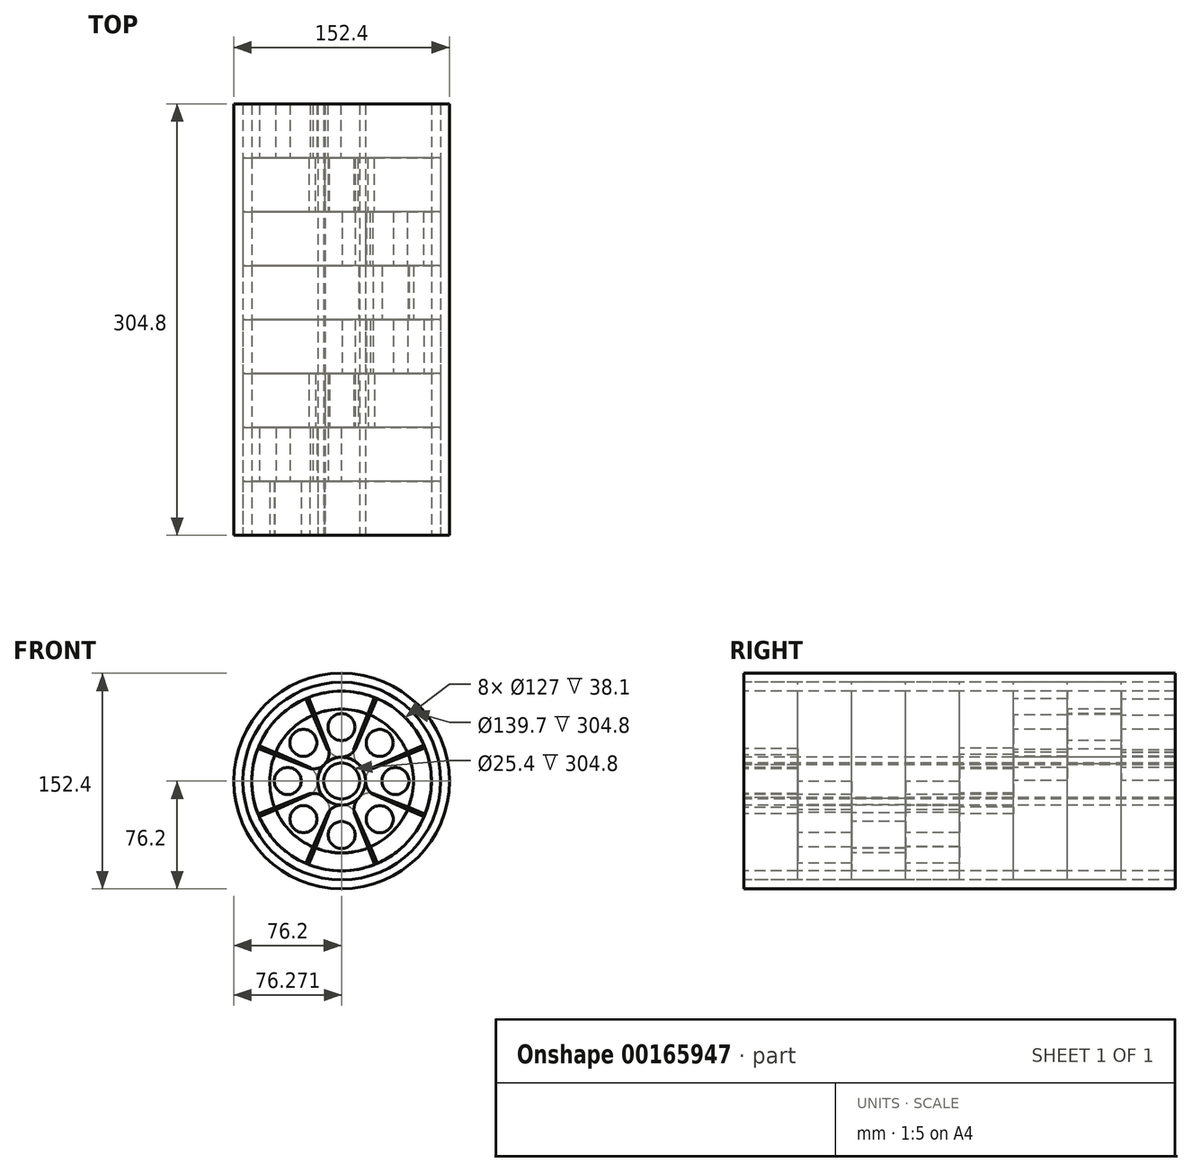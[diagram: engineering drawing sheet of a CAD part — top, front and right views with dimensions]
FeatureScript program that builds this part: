
annotation { "Feature Type Name" : "Feature", "Feature Type Description" : "" }
export const myFeature = defineFeature(function(context is Context, id is Id, definition is map)
    precondition{}
    {
        {
            var Q0;
            Q0=qCreatedBy(makeId("Front.planeOp"),FACE);
            var sketch = newSketch(context, id + "F0", { "sketchPlane" : qUnion([Q0])});
            skCircle(sketch, "E0", {"center": v(0, 0) * mm, "radius": 76.2 * mm});
            skCircle(sketch, "E1", {"center": v(0, 0) * mm, "radius": 63.5 * mm});
            skLineSegment(sketch, "E2", {"start": v(-47.23, -18.71) * mm, "end": v(-59.03, -23.4) * mm});
            skLineSegment(sketch, "E3", {"start": v(-47.15, 18.5) * mm, "end": v(-59.03, 23.21) * mm});
            skArc(sketch, "E4", {"start": v(-59.03, 23.21) * mm, "mid": v(-63.46, -0.1) * mm, "end": v(-59.03, -23.4) * mm});
            skArc(sketch, "E5", {"start": v(-47.15, 18.5) * mm, "mid": v(-50.76, -0.1) * mm, "end": v(-47.23, -18.71) * mm});
            skCircle(sketch, "E6", {"center": v(0.04, -0.1) * mm, "radius": 16.9 * mm});
            skLineSegment(sketch, "E7", {"start": v(-47.23, -18.71) * mm, "end": v(-15.66, -6.32) * mm});
            skLineSegment(sketch, "E8", {"start": v(-47.15, 18.5) * mm, "end": v(-15.65, 6.16) * mm});
            skCircle(sketch, "E9", {"center": v(0, 0) * mm, "radius": 12.7 * mm});
            skPoint(sketch, "E10.middle", {"position": v(-34.7, 0) * mm});
            skArc(sketch, "E11", {"start": v(-22.37, 8.8) * mm, "mid": v(-16.55, 9.06) * mm, "end": v(-11.6, 12.14) * mm});
            skArc(sketch, "E12", {"start": v(-11.6, -12.34) * mm, "mid": v(-16.54, -9.23) * mm, "end": v(-22.37, -8.95) * mm});
            skArc(sketch, "E13", {"start": v(-58.86, 23.14) * mm, "mid": v(-63.24, -0.1) * mm, "end": v(-58.8, -23.31) * mm});
            skCircle(sketch, "E14", {"center": v(-38.06, 0) * mm, "radius": 9.53 * mm});
            skCircle(sketch, "E15", {"center": v(0.07, 0) * mm, "radius": 69.85 * mm});
            skSolve(sketch);
        }
        {
            var Q0;
            Q0=makeQuery(id+"F0.imprint","IMPRINT",FACE,{"disambiguationData":[TD([[makeQuery(id+"F0.imprint","IMPRINT",EDGE,{"derivedFrom":sQuery(id+"F0.wireOp",EDGE,"dWqBjylU-pobx-G8Ro-5PX9-iFVg2W9Lq8eQ")}),1.0]])]});
            var Q1;
            Q1=makeQuery(id+"F0.imprint","IMPRINT",FACE,{"disambiguationData":[TD([[makeQuery(id+"F0.imprint","IMPRINT",EDGE,{"derivedFrom":sQuery(id+"F0.wireOp",EDGE,"E0")}),1.0]])]});
            extrude(context, id + "F1", {"entities" : qUnion([Q0, Q1]), "oppositeDirection" : true, "depth" : 304.8 * mm});
        }
        {
            var Q0;
            Q0=makeQuery(id+"F0.imprint","IMPRINT",FACE,{"disambiguationData":[TD([[makeQuery(id+"F0.imprint","IMPRINT",EDGE,{"derivedFrom":sQuery(id+"F0.wireOp",EDGE,"E2")}),-1.0]])]});
            extrude(context, id + "F2", {"entities" : qUnion([Q0]), "oppositeDirection" : true, "depth" : 38.1 * mm});
        }
        {
            var Q0;
            Q0=makeQuery(id+"F2.opExtrude","SWEPT_BODY",BODY,{"disambiguationData":[OSD([sQuery(id+"F0.wireOp",EDGE,"E2"),sQuery(id+"F0.wireOp",EDGE,"E3"),sQuery(id+"F0.wireOp",EDGE,"E4"),sQuery(id+"F0.wireOp",EDGE,"E5")])]});
            var Q1;
            Q1=makeQuery(id+"F1.opExtrude","CAP_EDGE",EDGE,{"disambiguationData":[OSD([sQuery(id+"F0.wireOp",EDGE,"E1")])],"isStart":true});
            transform(context, id + "F3", {"entities" : qUnion([Q0]), "transformType" : TransformType.TRANSLATION_3D, "dx" : 0 * mm, "dy" : 38.1 * mm, "dz" : 0 * mm, "makeCopy" : true});
        }
        {
            var Q0;
            Q0=makeQuery(id+"F3.opPattern","COPY",BODY,{"derivedFrom":makeQuery(id+"F2.opExtrude","SWEPT_BODY",BODY,{"disambiguationData":[OSD([sQuery(id+"F0.wireOp",EDGE,"E2"),sQuery(id+"F0.wireOp",EDGE,"E3"),sQuery(id+"F0.wireOp",EDGE,"E4"),sQuery(id+"F0.wireOp",EDGE,"E5")])]}),"instanceName":"1"});
            var Q1;
            Q1=makeQuery(id+"F1.opExtrude","CAP_EDGE",EDGE,{"disambiguationData":[OSD([sQuery(id+"F0.wireOp",EDGE,"E15")])],"isStart":true});
            transform(context, id + "F4", {"entities" : qUnion([Q0]), "transformType" : TransformType.ROTATION, "transformAxis" : qUnion([Q1]), "angle" : 45 * degree, "makeCopy" : false});
        }
        {
            var Q0;
            Q0=makeQuery(id+"F2.opExtrude","SWEPT_BODY",BODY,{"disambiguationData":[OSD([sQuery(id+"F0.wireOp",EDGE,"E2"),sQuery(id+"F0.wireOp",EDGE,"E3"),sQuery(id+"F0.wireOp",EDGE,"E4"),sQuery(id+"F0.wireOp",EDGE,"E5")])]});
            var Q1;
            Q1=makeQuery(id+"F3.opPattern","COPY",BODY,{"derivedFrom":makeQuery(id+"F2.opExtrude","SWEPT_BODY",BODY,{"disambiguationData":[OSD([sQuery(id+"F0.wireOp",EDGE,"E2"),sQuery(id+"F0.wireOp",EDGE,"E3"),sQuery(id+"F0.wireOp",EDGE,"E4"),sQuery(id+"F0.wireOp",EDGE,"E5")])]}),"instanceName":"1"});
            transform(context, id + "F5", {"entities" : qUnion([Q0, Q1]), "transformType" : TransformType.TRANSLATION_3D, "dx" : 0 * mm, "dy" : 76.2 * mm, "dz" : 0 * mm, "makeCopy" : true});
        }
        {
            var Q0;
            Q0=makeQuery(id+"F5.opPattern","COPY",BODY,{"derivedFrom":makeQuery(id+"F2.opExtrude","SWEPT_BODY",BODY,{"disambiguationData":[OSD([sQuery(id+"F0.wireOp",EDGE,"E2"),sQuery(id+"F0.wireOp",EDGE,"E3"),sQuery(id+"F0.wireOp",EDGE,"E4"),sQuery(id+"F0.wireOp",EDGE,"E5")])]}),"instanceName":"1"});
            var Q1;
            Q1=makeQuery(id+"F5.opPattern","COPY",BODY,{"derivedFrom":makeQuery(id+"F3.opPattern","COPY",BODY,{"derivedFrom":makeQuery(id+"F2.opExtrude","SWEPT_BODY",BODY,{"disambiguationData":[OSD([sQuery(id+"F0.wireOp",EDGE,"E2"),sQuery(id+"F0.wireOp",EDGE,"E3"),sQuery(id+"F0.wireOp",EDGE,"E4"),sQuery(id+"F0.wireOp",EDGE,"E5")])]}),"instanceName":"1"}),"instanceName":"1"});
            var Q2;
            Q2=makeQuery(id+"F1.opExtrude","CAP_EDGE",EDGE,{"disambiguationData":[OSD([sQuery(id+"F0.wireOp",EDGE,"E0")])],"isStart":true});
            transform(context, id + "F6", {"entities" : qUnion([Q0, Q1]), "transformType" : TransformType.ROTATION, "transformAxis" : qUnion([Q2]), "angle" : 90 * degree, "makeCopy" : false});
        }
        {
            var Q0;
            Q0=makeQuery(id+"F2.opExtrude","SWEPT_BODY",BODY,{"disambiguationData":[OSD([sQuery(id+"F0.wireOp",EDGE,"E2"),sQuery(id+"F0.wireOp",EDGE,"E3"),sQuery(id+"F0.wireOp",EDGE,"E4"),sQuery(id+"F0.wireOp",EDGE,"E5")])]});
            var Q1;
            Q1=makeQuery(id+"F3.opPattern","COPY",BODY,{"derivedFrom":makeQuery(id+"F2.opExtrude","SWEPT_BODY",BODY,{"disambiguationData":[OSD([sQuery(id+"F0.wireOp",EDGE,"E2"),sQuery(id+"F0.wireOp",EDGE,"E3"),sQuery(id+"F0.wireOp",EDGE,"E4"),sQuery(id+"F0.wireOp",EDGE,"E5")])]}),"instanceName":"1"});
            var Q2;
            Q2=makeQuery(id+"F5.opPattern","COPY",BODY,{"derivedFrom":makeQuery(id+"F2.opExtrude","SWEPT_BODY",BODY,{"disambiguationData":[OSD([sQuery(id+"F0.wireOp",EDGE,"E2"),sQuery(id+"F0.wireOp",EDGE,"E3"),sQuery(id+"F0.wireOp",EDGE,"E4"),sQuery(id+"F0.wireOp",EDGE,"E5")])]}),"instanceName":"1"});
            var Q3;
            Q3=makeQuery(id+"F5.opPattern","COPY",BODY,{"derivedFrom":makeQuery(id+"F3.opPattern","COPY",BODY,{"derivedFrom":makeQuery(id+"F2.opExtrude","SWEPT_BODY",BODY,{"disambiguationData":[OSD([sQuery(id+"F0.wireOp",EDGE,"E2"),sQuery(id+"F0.wireOp",EDGE,"E3"),sQuery(id+"F0.wireOp",EDGE,"E4"),sQuery(id+"F0.wireOp",EDGE,"E5")])]}),"instanceName":"1"}),"instanceName":"1"});
            transform(context, id + "F7", {"entities" : qUnion([Q0, Q1, Q2, Q3]), "transformType" : TransformType.TRANSLATION_3D, "dx" : 0 * mm, "dy" : 152.4 * mm, "dz" : 0 * mm, "makeCopy" : true});
        }
        {
            var Q0;
            Q0=makeQuery(id+"F7.opPattern","COPY",BODY,{"derivedFrom":makeQuery(id+"F2.opExtrude","SWEPT_BODY",BODY,{"disambiguationData":[OSD([sQuery(id+"F0.wireOp",EDGE,"E2"),sQuery(id+"F0.wireOp",EDGE,"E3"),sQuery(id+"F0.wireOp",EDGE,"E4"),sQuery(id+"F0.wireOp",EDGE,"E5")])]}),"instanceName":"1"});
            var Q1;
            Q1=makeQuery(id+"F7.opPattern","COPY",BODY,{"derivedFrom":makeQuery(id+"F3.opPattern","COPY",BODY,{"derivedFrom":makeQuery(id+"F2.opExtrude","SWEPT_BODY",BODY,{"disambiguationData":[OSD([sQuery(id+"F0.wireOp",EDGE,"E2"),sQuery(id+"F0.wireOp",EDGE,"E3"),sQuery(id+"F0.wireOp",EDGE,"E4"),sQuery(id+"F0.wireOp",EDGE,"E5")])]}),"instanceName":"1"}),"instanceName":"1"});
            var Q2;
            Q2=makeQuery(id+"F7.opPattern","COPY",BODY,{"derivedFrom":makeQuery(id+"F5.opPattern","COPY",BODY,{"derivedFrom":makeQuery(id+"F2.opExtrude","SWEPT_BODY",BODY,{"disambiguationData":[OSD([sQuery(id+"F0.wireOp",EDGE,"E2"),sQuery(id+"F0.wireOp",EDGE,"E3"),sQuery(id+"F0.wireOp",EDGE,"E4"),sQuery(id+"F0.wireOp",EDGE,"E5")])]}),"instanceName":"1"}),"instanceName":"1"});
            var Q3;
            Q3=makeQuery(id+"F7.opPattern","COPY",BODY,{"derivedFrom":makeQuery(id+"F5.opPattern","COPY",BODY,{"derivedFrom":makeQuery(id+"F3.opPattern","COPY",BODY,{"derivedFrom":makeQuery(id+"F2.opExtrude","SWEPT_BODY",BODY,{"disambiguationData":[OSD([sQuery(id+"F0.wireOp",EDGE,"E2"),sQuery(id+"F0.wireOp",EDGE,"E3"),sQuery(id+"F0.wireOp",EDGE,"E4"),sQuery(id+"F0.wireOp",EDGE,"E5")])]}),"instanceName":"1"}),"instanceName":"1"}),"instanceName":"1"});
            var Q4;
            Q4=makeQuery(id+"F1.opExtrude","CAP_EDGE",EDGE,{"disambiguationData":[OSD([sQuery(id+"F0.wireOp",EDGE,"E0")])],"isStart":true});
            transform(context, id + "F8", {"entities" : qUnion([Q0, Q1, Q2, Q3]), "transformType" : TransformType.ROTATION, "transformAxis" : qUnion([Q4]), "angle" : 180 * degree, "makeCopy" : false});
        }
        {
            var Q0;
            Q0=makeQuery(id+"F0.imprint","IMPRINT",FACE,{"disambiguationData":[TD([[makeQuery(id+"F0.imprint","IMPRINT",EDGE,{"derivedFrom":sQuery(id+"F0.wireOp",EDGE,"E5")}),1.0]])]});
            var Q1;
            {var subQ0=sQuery(id+"F0.wireOp",EDGE,"E8");var subQ1=sQuery(id+"F0.wireOp",EDGE,"E6");var subQ2=makeQuery(id+"F0.imprint","INTERSECT",VERTEX,{"derivedFrom":[subQ1,subQ0]});Q1=makeQuery(id+"F0.imprint","IMPRINT",FACE,{"disambiguationData":[TD([[makeQuery(id+"F0.imprint","IMPRINT",EDGE,{"disambiguationData":[TD([[subQ2,1.0]])],"derivedFrom":subQ1}),-1.0]])]});}
            var Q2;
            {var subQ0=sQuery(id+"F0.wireOp",EDGE,"E7");var subQ1=sQuery(id+"F0.wireOp",EDGE,"E6");var subQ2=makeQuery(id+"F0.imprint","INTERSECT",VERTEX,{"derivedFrom":[subQ1,subQ0]});Q2=makeQuery(id+"F0.imprint","IMPRINT",FACE,{"disambiguationData":[TD([[makeQuery(id+"F0.imprint","IMPRINT",EDGE,{"disambiguationData":[TD([[subQ2,-1.0]])],"derivedFrom":subQ1}),-1.0]])]});}
            extrude(context, id + "F9", {"entities" : qUnion([Q0, Q1, Q2]), "oppositeDirection" : true, "depth" : 38.1 * mm});
        }
        {
            var Q0;
            Q0=makeQuery(id+"F9.opExtrude","SWEPT_BODY",BODY,{"disambiguationData":[OSD([sQuery(id+"F0.wireOp",EDGE,"E5"),sQuery(id+"F0.wireOp",EDGE,"E6"),sQuery(id+"F0.wireOp",EDGE,"E7"),sQuery(id+"F0.wireOp",EDGE,"E8"),sQuery(id+"F0.wireOp",EDGE,"4N7eOMkn-36Zl-0K50-I79r-F5F3qFzNZoCP"),sQuery(id+"F0.wireOp",EDGE,"E11"),sQuery(id+"F0.wireOp",EDGE,"E12")])]});
            transform(context, id + "F10", {"entities" : qUnion([Q0]), "transformType" : TransformType.TRANSLATION_3D, "dx" : 0 * mm, "dy" : 38.1 * mm, "dz" : 0 * mm, "makeCopy" : true});
        }
        {
            var Q0;
            Q0=makeQuery(id+"F10.opPattern","COPY",BODY,{"derivedFrom":makeQuery(id+"F9.opExtrude","SWEPT_BODY",BODY,{"disambiguationData":[OSD([sQuery(id+"F0.wireOp",EDGE,"E5"),sQuery(id+"F0.wireOp",EDGE,"E6"),sQuery(id+"F0.wireOp",EDGE,"E7"),sQuery(id+"F0.wireOp",EDGE,"E8"),sQuery(id+"F0.wireOp",EDGE,"4N7eOMkn-36Zl-0K50-I79r-F5F3qFzNZoCP"),sQuery(id+"F0.wireOp",EDGE,"E11"),sQuery(id+"F0.wireOp",EDGE,"E12")])]}),"instanceName":"1"});
            var Q1;
            Q1=makeQuery(id+"F1.opExtrude","CAP_EDGE",EDGE,{"disambiguationData":[OSD([sQuery(id+"F0.wireOp",EDGE,"E0")])],"isStart":true});
            transform(context, id + "F11", {"entities" : qUnion([Q0]), "transformType" : TransformType.ROTATION, "transformAxis" : qUnion([Q1]), "angle" : 45 * degree, "makeCopy" : false});
        }
        {
            var Q0;
            Q0=makeQuery(id+"F9.opExtrude","SWEPT_BODY",BODY,{"disambiguationData":[OSD([sQuery(id+"F0.wireOp",EDGE,"E5"),sQuery(id+"F0.wireOp",EDGE,"E6"),sQuery(id+"F0.wireOp",EDGE,"E7"),sQuery(id+"F0.wireOp",EDGE,"E8"),sQuery(id+"F0.wireOp",EDGE,"4N7eOMkn-36Zl-0K50-I79r-F5F3qFzNZoCP"),sQuery(id+"F0.wireOp",EDGE,"E11"),sQuery(id+"F0.wireOp",EDGE,"E12")])]});
            var Q1;
            Q1=makeQuery(id+"F10.opPattern","COPY",BODY,{"derivedFrom":makeQuery(id+"F9.opExtrude","SWEPT_BODY",BODY,{"disambiguationData":[OSD([sQuery(id+"F0.wireOp",EDGE,"E5"),sQuery(id+"F0.wireOp",EDGE,"E6"),sQuery(id+"F0.wireOp",EDGE,"E7"),sQuery(id+"F0.wireOp",EDGE,"E8"),sQuery(id+"F0.wireOp",EDGE,"4N7eOMkn-36Zl-0K50-I79r-F5F3qFzNZoCP"),sQuery(id+"F0.wireOp",EDGE,"E11"),sQuery(id+"F0.wireOp",EDGE,"E12")])]}),"instanceName":"1"});
            transform(context, id + "F12", {"entities" : qUnion([Q0, Q1]), "transformType" : TransformType.TRANSLATION_3D, "dx" : 0 * mm, "dy" : 76.2 * mm, "dz" : 0 * mm, "makeCopy" : true});
        }
        {
            var Q0;
            Q0=makeQuery(id+"F12.opPattern","COPY",BODY,{"derivedFrom":makeQuery(id+"F9.opExtrude","SWEPT_BODY",BODY,{"disambiguationData":[OSD([sQuery(id+"F0.wireOp",EDGE,"E5"),sQuery(id+"F0.wireOp",EDGE,"E6"),sQuery(id+"F0.wireOp",EDGE,"E7"),sQuery(id+"F0.wireOp",EDGE,"E8"),sQuery(id+"F0.wireOp",EDGE,"4N7eOMkn-36Zl-0K50-I79r-F5F3qFzNZoCP"),sQuery(id+"F0.wireOp",EDGE,"E11"),sQuery(id+"F0.wireOp",EDGE,"E12")])]}),"instanceName":"1"});
            var Q1;
            Q1=makeQuery(id+"F12.opPattern","COPY",BODY,{"derivedFrom":makeQuery(id+"F10.opPattern","COPY",BODY,{"derivedFrom":makeQuery(id+"F9.opExtrude","SWEPT_BODY",BODY,{"disambiguationData":[OSD([sQuery(id+"F0.wireOp",EDGE,"E5"),sQuery(id+"F0.wireOp",EDGE,"E6"),sQuery(id+"F0.wireOp",EDGE,"E7"),sQuery(id+"F0.wireOp",EDGE,"E8"),sQuery(id+"F0.wireOp",EDGE,"4N7eOMkn-36Zl-0K50-I79r-F5F3qFzNZoCP"),sQuery(id+"F0.wireOp",EDGE,"E11"),sQuery(id+"F0.wireOp",EDGE,"E12")])]}),"instanceName":"1"}),"instanceName":"1"});
            var Q2;
            Q2=makeQuery(id+"F1.opExtrude","CAP_EDGE",EDGE,{"disambiguationData":[OSD([sQuery(id+"F0.wireOp",EDGE,"E15")])],"isStart":true});
            transform(context, id + "F13", {"entities" : qUnion([Q0, Q1]), "transformType" : TransformType.ROTATION, "transformAxis" : qUnion([Q2]), "angle" : 90 * degree, "makeCopy" : false});
        }
        {
            var Q0;
            Q0=makeQuery(id+"F9.opExtrude","SWEPT_BODY",BODY,{"disambiguationData":[OSD([sQuery(id+"F0.wireOp",EDGE,"E5"),sQuery(id+"F0.wireOp",EDGE,"E6"),sQuery(id+"F0.wireOp",EDGE,"E7"),sQuery(id+"F0.wireOp",EDGE,"E8"),sQuery(id+"F0.wireOp",EDGE,"4N7eOMkn-36Zl-0K50-I79r-F5F3qFzNZoCP"),sQuery(id+"F0.wireOp",EDGE,"E11"),sQuery(id+"F0.wireOp",EDGE,"E12")])]});
            var Q1;
            Q1=makeQuery(id+"F10.opPattern","COPY",BODY,{"derivedFrom":makeQuery(id+"F9.opExtrude","SWEPT_BODY",BODY,{"disambiguationData":[OSD([sQuery(id+"F0.wireOp",EDGE,"E5"),sQuery(id+"F0.wireOp",EDGE,"E6"),sQuery(id+"F0.wireOp",EDGE,"E7"),sQuery(id+"F0.wireOp",EDGE,"E8"),sQuery(id+"F0.wireOp",EDGE,"4N7eOMkn-36Zl-0K50-I79r-F5F3qFzNZoCP"),sQuery(id+"F0.wireOp",EDGE,"E11"),sQuery(id+"F0.wireOp",EDGE,"E12")])]}),"instanceName":"1"});
            var Q2;
            Q2=makeQuery(id+"F12.opPattern","COPY",BODY,{"derivedFrom":makeQuery(id+"F9.opExtrude","SWEPT_BODY",BODY,{"disambiguationData":[OSD([sQuery(id+"F0.wireOp",EDGE,"E5"),sQuery(id+"F0.wireOp",EDGE,"E6"),sQuery(id+"F0.wireOp",EDGE,"E7"),sQuery(id+"F0.wireOp",EDGE,"E8"),sQuery(id+"F0.wireOp",EDGE,"4N7eOMkn-36Zl-0K50-I79r-F5F3qFzNZoCP"),sQuery(id+"F0.wireOp",EDGE,"E11"),sQuery(id+"F0.wireOp",EDGE,"E12")])]}),"instanceName":"1"});
            var Q3;
            Q3=makeQuery(id+"F12.opPattern","COPY",BODY,{"derivedFrom":makeQuery(id+"F10.opPattern","COPY",BODY,{"derivedFrom":makeQuery(id+"F9.opExtrude","SWEPT_BODY",BODY,{"disambiguationData":[OSD([sQuery(id+"F0.wireOp",EDGE,"E5"),sQuery(id+"F0.wireOp",EDGE,"E6"),sQuery(id+"F0.wireOp",EDGE,"E7"),sQuery(id+"F0.wireOp",EDGE,"E8"),sQuery(id+"F0.wireOp",EDGE,"4N7eOMkn-36Zl-0K50-I79r-F5F3qFzNZoCP"),sQuery(id+"F0.wireOp",EDGE,"E11"),sQuery(id+"F0.wireOp",EDGE,"E12")])]}),"instanceName":"1"}),"instanceName":"1"});
            transform(context, id + "F14", {"entities" : qUnion([Q0, Q1, Q2, Q3]), "transformType" : TransformType.TRANSLATION_3D, "dx" : 0 * mm, "dy" : 152.4 * mm, "dz" : 0 * mm, "makeCopy" : true});
        }
        {
            var Q0;
            Q0=makeQuery(id+"F14.opPattern","COPY",BODY,{"derivedFrom":makeQuery(id+"F9.opExtrude","SWEPT_BODY",BODY,{"disambiguationData":[OSD([sQuery(id+"F0.wireOp",EDGE,"E5"),sQuery(id+"F0.wireOp",EDGE,"E6"),sQuery(id+"F0.wireOp",EDGE,"E7"),sQuery(id+"F0.wireOp",EDGE,"E8"),sQuery(id+"F0.wireOp",EDGE,"4N7eOMkn-36Zl-0K50-I79r-F5F3qFzNZoCP"),sQuery(id+"F0.wireOp",EDGE,"E11"),sQuery(id+"F0.wireOp",EDGE,"E12")])]}),"instanceName":"1"});
            var Q1;
            Q1=makeQuery(id+"F14.opPattern","COPY",BODY,{"derivedFrom":makeQuery(id+"F10.opPattern","COPY",BODY,{"derivedFrom":makeQuery(id+"F9.opExtrude","SWEPT_BODY",BODY,{"disambiguationData":[OSD([sQuery(id+"F0.wireOp",EDGE,"E5"),sQuery(id+"F0.wireOp",EDGE,"E6"),sQuery(id+"F0.wireOp",EDGE,"E7"),sQuery(id+"F0.wireOp",EDGE,"E8"),sQuery(id+"F0.wireOp",EDGE,"4N7eOMkn-36Zl-0K50-I79r-F5F3qFzNZoCP"),sQuery(id+"F0.wireOp",EDGE,"E11"),sQuery(id+"F0.wireOp",EDGE,"E12")])]}),"instanceName":"1"}),"instanceName":"1"});
            var Q2;
            Q2=makeQuery(id+"F14.opPattern","COPY",BODY,{"derivedFrom":makeQuery(id+"F12.opPattern","COPY",BODY,{"derivedFrom":makeQuery(id+"F9.opExtrude","SWEPT_BODY",BODY,{"disambiguationData":[OSD([sQuery(id+"F0.wireOp",EDGE,"E5"),sQuery(id+"F0.wireOp",EDGE,"E6"),sQuery(id+"F0.wireOp",EDGE,"E7"),sQuery(id+"F0.wireOp",EDGE,"E8"),sQuery(id+"F0.wireOp",EDGE,"4N7eOMkn-36Zl-0K50-I79r-F5F3qFzNZoCP"),sQuery(id+"F0.wireOp",EDGE,"E11"),sQuery(id+"F0.wireOp",EDGE,"E12")])]}),"instanceName":"1"}),"instanceName":"1"});
            var Q3;
            Q3=makeQuery(id+"F14.opPattern","COPY",BODY,{"derivedFrom":makeQuery(id+"F12.opPattern","COPY",BODY,{"derivedFrom":makeQuery(id+"F10.opPattern","COPY",BODY,{"derivedFrom":makeQuery(id+"F9.opExtrude","SWEPT_BODY",BODY,{"disambiguationData":[OSD([sQuery(id+"F0.wireOp",EDGE,"E5"),sQuery(id+"F0.wireOp",EDGE,"E6"),sQuery(id+"F0.wireOp",EDGE,"E7"),sQuery(id+"F0.wireOp",EDGE,"E8"),sQuery(id+"F0.wireOp",EDGE,"4N7eOMkn-36Zl-0K50-I79r-F5F3qFzNZoCP"),sQuery(id+"F0.wireOp",EDGE,"E11"),sQuery(id+"F0.wireOp",EDGE,"E12")])]}),"instanceName":"1"}),"instanceName":"1"}),"instanceName":"1"});
            var Q4;
            Q4=makeQuery(id+"F1.opExtrude","CAP_EDGE",EDGE,{"disambiguationData":[OSD([sQuery(id+"F0.wireOp",EDGE,"E0")])],"isStart":true});
            transform(context, id + "F15", {"entities" : qUnion([Q0, Q1, Q2, Q3]), "transformType" : TransformType.ROTATION, "transformAxis" : qUnion([Q4]), "angle" : 180 * degree, "makeCopy" : false});
        }
        {
            var Q0;
            Q0=makeQuery(id+"F0.imprint","IMPRINT",FACE,{"disambiguationData":[TD([[makeQuery(id+"F0.imprint","IMPRINT",EDGE,{"derivedFrom":sQuery(id+"F0.wireOp",EDGE,"E9")}),-1.0]])]});
            extrude(context, id + "F16", {"entities" : qUnion([Q0]), "oppositeDirection" : true, "depth" : 304.8 * mm});
        }
        {
            var Q0;
            Q0=makeQuery(id+"F0.imprint","IMPRINT",FACE,{"disambiguationData":[TD([[makeQuery(id+"F0.imprint","IMPRINT",EDGE,{"derivedFrom":sQuery(id+"F0.wireOp",EDGE,"E1")}),-1.0]])]});
            extrude(context, id + "F17", {"entities" : qUnion([Q0]), "oppositeDirection" : true, "depth" : 38.1 * mm});
        }
        {
            var Q0;
            Q0=makeQuery(id+"F17.opExtrude","SWEPT_BODY",BODY,{"disambiguationData":[OSD([sQuery(id+"F0.wireOp",EDGE,"E1"),sQuery(id+"F0.wireOp",EDGE,"E15")])]});
            transform(context, id + "F18", {"entities" : qUnion([Q0]), "transformType" : TransformType.TRANSLATION_3D, "dx" : 0 * mm, "dy" : 38.1 * mm, "dz" : 0 * mm, "makeCopy" : true});
        }
        {
            var Q0;
            Q0=makeQuery(id+"F17.opExtrude","SWEPT_BODY",BODY,{"disambiguationData":[OSD([sQuery(id+"F0.wireOp",EDGE,"E1"),sQuery(id+"F0.wireOp",EDGE,"E15")])]});
            var Q1;
            Q1=makeQuery(id+"F18.opPattern","COPY",BODY,{"derivedFrom":makeQuery(id+"F17.opExtrude","SWEPT_BODY",BODY,{"disambiguationData":[OSD([sQuery(id+"F0.wireOp",EDGE,"E1"),sQuery(id+"F0.wireOp",EDGE,"E15")])]}),"instanceName":"1"});
            transform(context, id + "F19", {"entities" : qUnion([Q0, Q1]), "transformType" : TransformType.TRANSLATION_3D, "dx" : 0 * mm, "dy" : 76.2 * mm, "dz" : 0 * mm, "makeCopy" : true});
        }
        {
            var Q0;
            Q0=makeQuery(id+"F17.opExtrude","SWEPT_BODY",BODY,{"disambiguationData":[OSD([sQuery(id+"F0.wireOp",EDGE,"E1"),sQuery(id+"F0.wireOp",EDGE,"E15")])]});
            var Q1;
            Q1=makeQuery(id+"F18.opPattern","COPY",BODY,{"derivedFrom":makeQuery(id+"F17.opExtrude","SWEPT_BODY",BODY,{"disambiguationData":[OSD([sQuery(id+"F0.wireOp",EDGE,"E1"),sQuery(id+"F0.wireOp",EDGE,"E15")])]}),"instanceName":"1"});
            var Q2;
            Q2=makeQuery(id+"F19.opPattern","COPY",BODY,{"derivedFrom":makeQuery(id+"F17.opExtrude","SWEPT_BODY",BODY,{"disambiguationData":[OSD([sQuery(id+"F0.wireOp",EDGE,"E1"),sQuery(id+"F0.wireOp",EDGE,"E15")])]}),"instanceName":"1"});
            var Q3;
            Q3=makeQuery(id+"F19.opPattern","COPY",BODY,{"derivedFrom":makeQuery(id+"F18.opPattern","COPY",BODY,{"derivedFrom":makeQuery(id+"F17.opExtrude","SWEPT_BODY",BODY,{"disambiguationData":[OSD([sQuery(id+"F0.wireOp",EDGE,"E1"),sQuery(id+"F0.wireOp",EDGE,"E15")])]}),"instanceName":"1"}),"instanceName":"1"});
            transform(context, id + "F20", {"entities" : qUnion([Q0, Q1, Q2, Q3]), "transformType" : TransformType.TRANSLATION_3D, "dx" : 0 * mm, "dy" : 152.4 * mm, "dz" : 0 * mm, "makeCopy" : true});
        }
        {
            var Q0;
            Q0=makeQuery(id+"F2.opExtrude","SWEPT_EDGE",EDGE,{"disambiguationData":[OSD([sQuery(id+"F0.wireOp",EDGE,"E3"),sQuery(id+"F0.wireOp",EDGE,"E4")])]});
            var Q1;
            Q1=makeQuery(id+"F2.opExtrude","SWEPT_EDGE",EDGE,{"disambiguationData":[OSD([sQuery(id+"F0.wireOp",EDGE,"E1"),sQuery(id+"F0.wireOp",EDGE,"E2"),sQuery(id+"F0.wireOp",EDGE,"E4")])]});
            var Q2;
            Q2=makeQuery(id+"F3.opPattern","COPY",EDGE,{"derivedFrom":makeQuery(id+"F2.opExtrude","SWEPT_EDGE",EDGE,{"disambiguationData":[OSD([sQuery(id+"F0.wireOp",EDGE,"E3"),sQuery(id+"F0.wireOp",EDGE,"E4")])]}),"instanceName":"1"});
            var Q3;
            Q3=makeQuery(id+"F3.opPattern","COPY",EDGE,{"derivedFrom":makeQuery(id+"F2.opExtrude","SWEPT_EDGE",EDGE,{"disambiguationData":[OSD([sQuery(id+"F0.wireOp",EDGE,"E1"),sQuery(id+"F0.wireOp",EDGE,"E2"),sQuery(id+"F0.wireOp",EDGE,"E4")])]}),"instanceName":"1"});
            var Q4;
            Q4=makeQuery(id+"F5.opPattern","COPY",EDGE,{"derivedFrom":makeQuery(id+"F2.opExtrude","SWEPT_EDGE",EDGE,{"disambiguationData":[OSD([sQuery(id+"F0.wireOp",EDGE,"E3"),sQuery(id+"F0.wireOp",EDGE,"E4")])]}),"instanceName":"1"});
            var Q5;
            Q5=makeQuery(id+"F5.opPattern","COPY",EDGE,{"derivedFrom":makeQuery(id+"F2.opExtrude","SWEPT_EDGE",EDGE,{"disambiguationData":[OSD([sQuery(id+"F0.wireOp",EDGE,"E1"),sQuery(id+"F0.wireOp",EDGE,"E2"),sQuery(id+"F0.wireOp",EDGE,"E4")])]}),"instanceName":"1"});
            var Q6;
            Q6=makeQuery(id+"F5.opPattern","COPY",EDGE,{"derivedFrom":makeQuery(id+"F3.opPattern","COPY",EDGE,{"derivedFrom":makeQuery(id+"F2.opExtrude","SWEPT_EDGE",EDGE,{"disambiguationData":[OSD([sQuery(id+"F0.wireOp",EDGE,"E1"),sQuery(id+"F0.wireOp",EDGE,"E2"),sQuery(id+"F0.wireOp",EDGE,"E4")])]}),"instanceName":"1"}),"instanceName":"1"});
            var Q7;
            Q7=makeQuery(id+"F5.opPattern","COPY",EDGE,{"derivedFrom":makeQuery(id+"F3.opPattern","COPY",EDGE,{"derivedFrom":makeQuery(id+"F2.opExtrude","SWEPT_EDGE",EDGE,{"disambiguationData":[OSD([sQuery(id+"F0.wireOp",EDGE,"E3"),sQuery(id+"F0.wireOp",EDGE,"E4")])]}),"instanceName":"1"}),"instanceName":"1"});
            var Q8;
            Q8=makeQuery(id+"F7.opPattern","COPY",EDGE,{"derivedFrom":makeQuery(id+"F2.opExtrude","SWEPT_EDGE",EDGE,{"disambiguationData":[OSD([sQuery(id+"F0.wireOp",EDGE,"E3"),sQuery(id+"F0.wireOp",EDGE,"E4")])]}),"instanceName":"1"});
            var Q9;
            Q9=makeQuery(id+"F7.opPattern","COPY",EDGE,{"derivedFrom":makeQuery(id+"F2.opExtrude","SWEPT_EDGE",EDGE,{"disambiguationData":[OSD([sQuery(id+"F0.wireOp",EDGE,"E1"),sQuery(id+"F0.wireOp",EDGE,"E2"),sQuery(id+"F0.wireOp",EDGE,"E4")])]}),"instanceName":"1"});
            var Q10;
            Q10=makeQuery(id+"F7.opPattern","COPY",EDGE,{"derivedFrom":makeQuery(id+"F3.opPattern","COPY",EDGE,{"derivedFrom":makeQuery(id+"F2.opExtrude","SWEPT_EDGE",EDGE,{"disambiguationData":[OSD([sQuery(id+"F0.wireOp",EDGE,"E1"),sQuery(id+"F0.wireOp",EDGE,"E2"),sQuery(id+"F0.wireOp",EDGE,"E4")])]}),"instanceName":"1"}),"instanceName":"1"});
            var Q11;
            Q11=makeQuery(id+"F7.opPattern","COPY",EDGE,{"derivedFrom":makeQuery(id+"F3.opPattern","COPY",EDGE,{"derivedFrom":makeQuery(id+"F2.opExtrude","SWEPT_EDGE",EDGE,{"disambiguationData":[OSD([sQuery(id+"F0.wireOp",EDGE,"E3"),sQuery(id+"F0.wireOp",EDGE,"E4")])]}),"instanceName":"1"}),"instanceName":"1"});
            var Q12;
            Q12=makeQuery(id+"F7.opPattern","COPY",EDGE,{"derivedFrom":makeQuery(id+"F5.opPattern","COPY",EDGE,{"derivedFrom":makeQuery(id+"F2.opExtrude","SWEPT_EDGE",EDGE,{"disambiguationData":[OSD([sQuery(id+"F0.wireOp",EDGE,"E3"),sQuery(id+"F0.wireOp",EDGE,"E4")])]}),"instanceName":"1"}),"instanceName":"1"});
            var Q13;
            Q13=makeQuery(id+"F7.opPattern","COPY",EDGE,{"derivedFrom":makeQuery(id+"F5.opPattern","COPY",EDGE,{"derivedFrom":makeQuery(id+"F2.opExtrude","SWEPT_EDGE",EDGE,{"disambiguationData":[OSD([sQuery(id+"F0.wireOp",EDGE,"E1"),sQuery(id+"F0.wireOp",EDGE,"E2"),sQuery(id+"F0.wireOp",EDGE,"E4")])]}),"instanceName":"1"}),"instanceName":"1"});
            var Q14;
            Q14=makeQuery(id+"F7.opPattern","COPY",EDGE,{"derivedFrom":makeQuery(id+"F5.opPattern","COPY",EDGE,{"derivedFrom":makeQuery(id+"F3.opPattern","COPY",EDGE,{"derivedFrom":makeQuery(id+"F2.opExtrude","SWEPT_EDGE",EDGE,{"disambiguationData":[OSD([sQuery(id+"F0.wireOp",EDGE,"E1"),sQuery(id+"F0.wireOp",EDGE,"E2"),sQuery(id+"F0.wireOp",EDGE,"E4")])]}),"instanceName":"1"}),"instanceName":"1"}),"instanceName":"1"});
            var Q15;
            Q15=makeQuery(id+"F7.opPattern","COPY",EDGE,{"derivedFrom":makeQuery(id+"F5.opPattern","COPY",EDGE,{"derivedFrom":makeQuery(id+"F3.opPattern","COPY",EDGE,{"derivedFrom":makeQuery(id+"F2.opExtrude","SWEPT_EDGE",EDGE,{"disambiguationData":[OSD([sQuery(id+"F0.wireOp",EDGE,"E3"),sQuery(id+"F0.wireOp",EDGE,"E4")])]}),"instanceName":"1"}),"instanceName":"1"}),"instanceName":"1"});
            fillet(context, id + "F21", {"entities" : qUnion([Q0, Q1, Q2, Q3, Q4, Q5, Q6, Q7, Q8, Q9, Q10, Q11, Q12, Q13, Q14, Q15]), "radius" : 0.5 * mm, "tangentPropagation" : true, "allowEdgeOverflow" : false});
        }
    });
